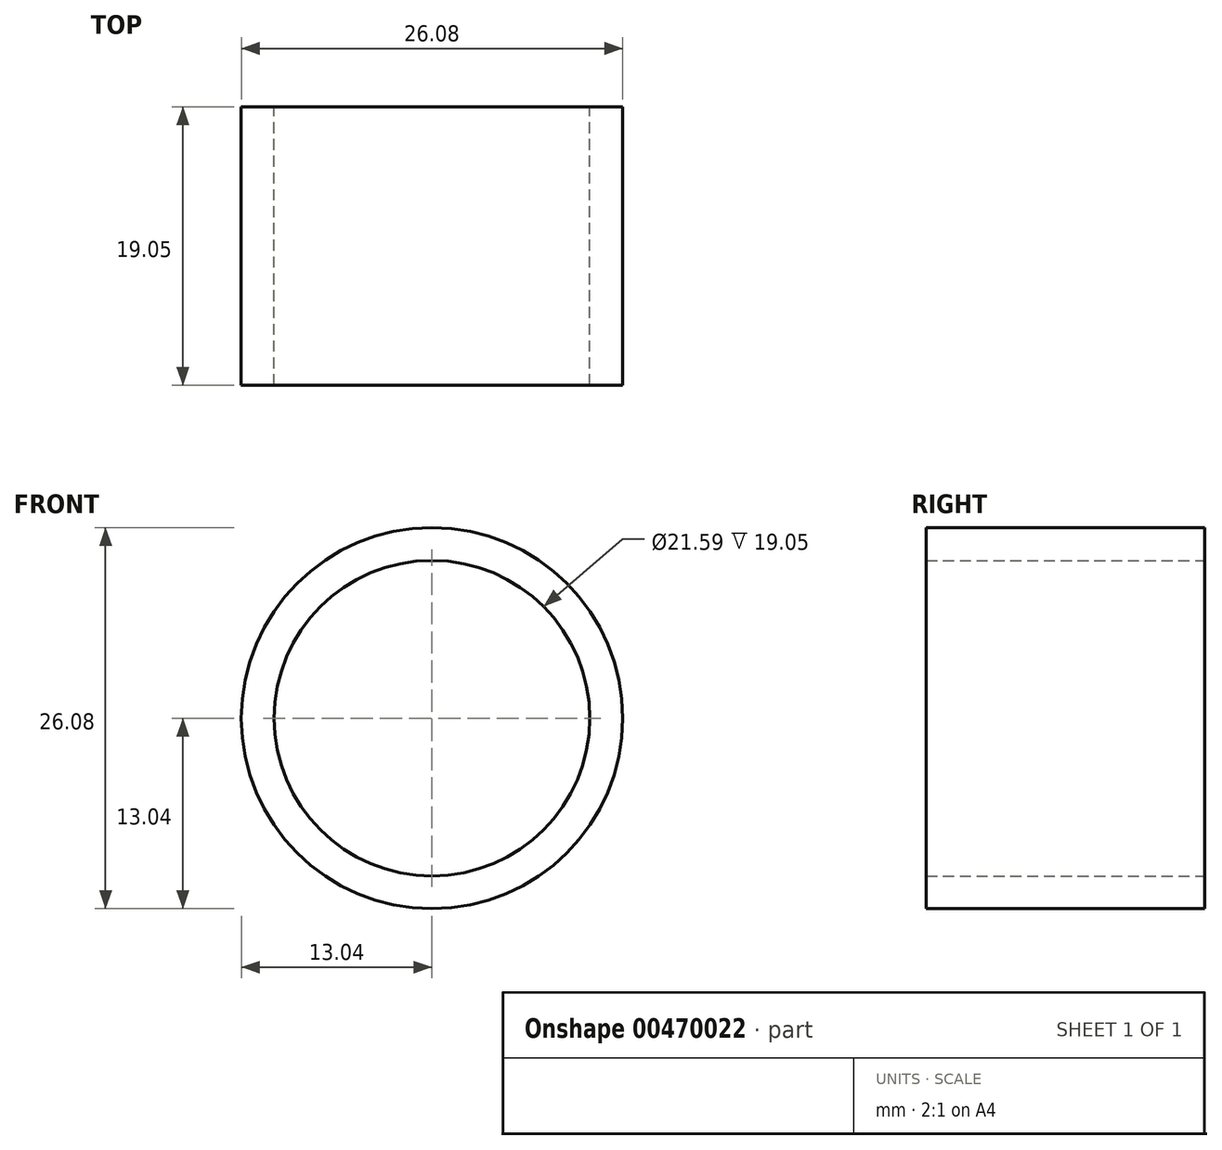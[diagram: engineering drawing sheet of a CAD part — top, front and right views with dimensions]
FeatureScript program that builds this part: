
annotation { "Feature Type Name" : "Feature", "Feature Type Description" : "" }
export const myFeature = defineFeature(function(context is Context, id is Id, definition is map)
    precondition{}
    {
        {
            var Q0;
            Q0=qCreatedBy(makeId("Front.planeOp"),FACE);
            var sketch = newSketch(context, id + "F0", { "sketchPlane" : qUnion([Q0])});
            skCircle(sketch, "E0", {"center": v(0, 0) * mm, "radius": 10.8 * mm});
            skCircle(sketch, "E1", {"center": v(0, 0) * mm, "radius": 13.04 * mm});
            skSolve(sketch);
        }
        {
            var Q0;
            Q0 = qSketchRegion(id + "F0", true);
            extrude(context, id + "F1", {"entities" : qUnion([Q0]), "depth" : 19.05 * mm});
        }
    });
